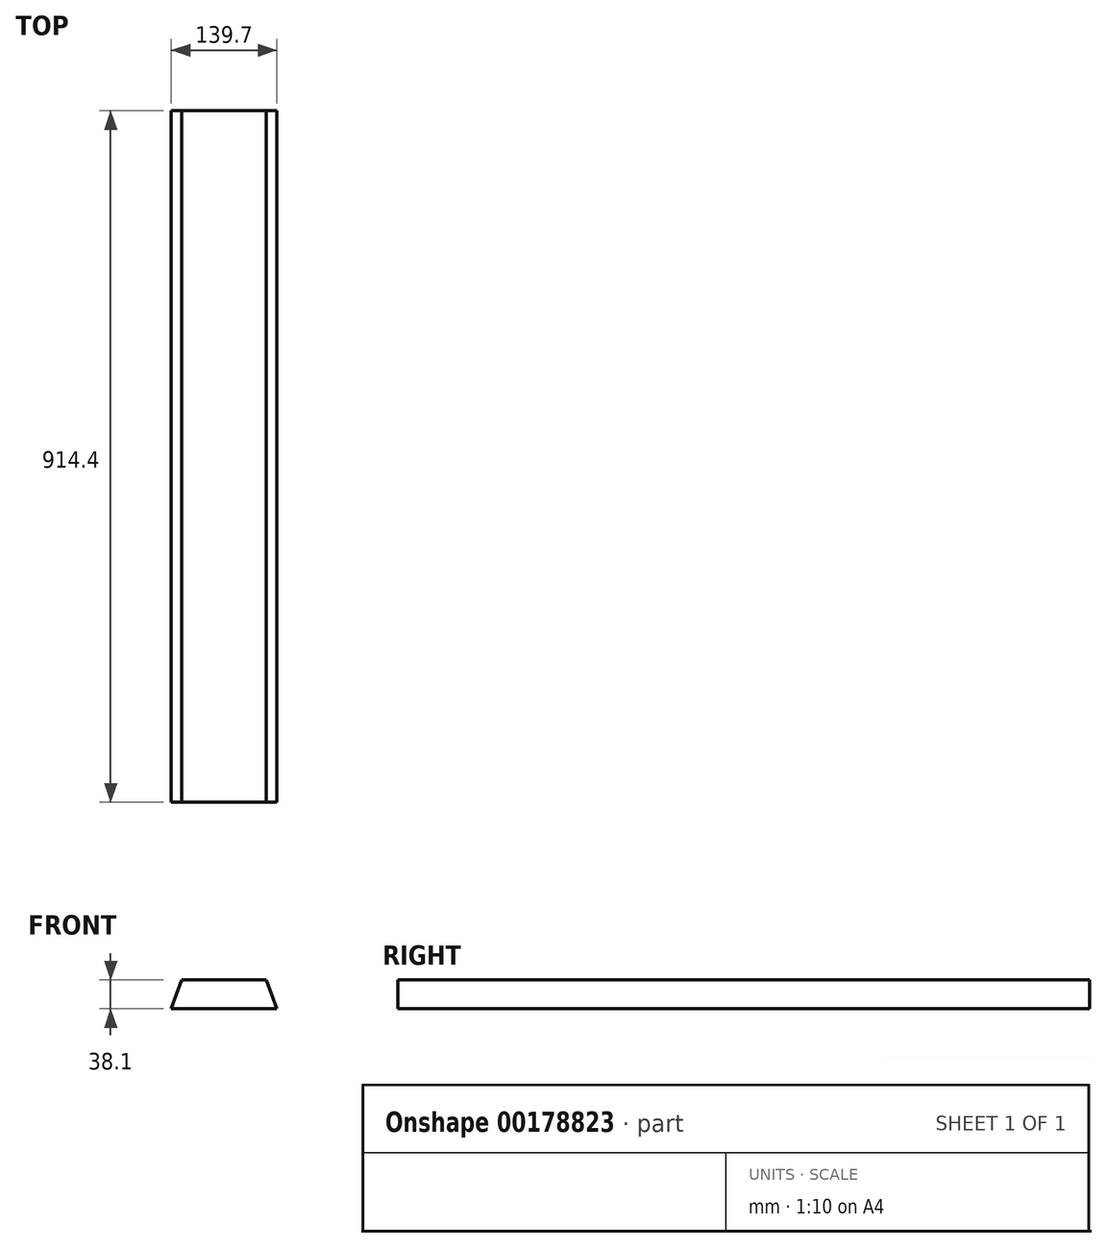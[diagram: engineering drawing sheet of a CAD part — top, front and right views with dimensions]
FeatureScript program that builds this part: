
annotation { "Feature Type Name" : "Feature", "Feature Type Description" : "" }
export const myFeature = defineFeature(function(context is Context, id is Id, definition is map)
    precondition{}
    {
        {
            var Q0;
            Q0=qCreatedBy(makeId("Front.planeOp"),FACE);
            var sketch = newSketch(context, id + "F0", { "sketchPlane" : qUnion([Q0])});
            skLineSegment(sketch, "E0.bottom", {"start": v(0, 0) * mm, "end": v(139.7, 0) * mm});
            skLineSegment(sketch, "E0.top", {"start": v(0, 38.1) * mm, "end": v(139.7, 38.1) * mm});
            skLineSegment(sketch, "E0.left", {"start": v(0, 0) * mm, "end": v(0, 38.1) * mm});
            skLineSegment(sketch, "E0.right", {"start": v(139.7, 0) * mm, "end": v(139.7, 38.1) * mm});
            skSolve(sketch);
        }
        {
            var Q0;
            Q0 = qSketchRegion(id + "F0", true);
            extrude(context, id + "F1", {"entities" : qUnion([Q0]), "depth" : 914.4 * mm});
        }
        {
            var Q0;
            Q0=makeQuery(id+"F1.opExtrude","CAP_FACE",FACE,{"disambiguationData":[OSD([sQuery(id+"F0.wireOp",EDGE,"E0.bottom"),sQuery(id+"F0.wireOp",EDGE,"E0.top"),sQuery(id+"F0.wireOp",EDGE,"E0.left"),sQuery(id+"F0.wireOp",EDGE,"E0.right")])],"isStart":false});
            var sketch = newSketch(context, id + "F2", { "sketchPlane" : qUnion([Q0])});
            skLineSegment(sketch, "E1", {"start": v(0, 0) * mm, "end": v(13.87, 38.1) * mm});
            skLineSegment(sketch, "E2", {"start": v(13.87, 38.1) * mm, "end": v(0, 38.1) * mm});
            skLineSegment(sketch, "E3", {"start": v(0, 38.1) * mm, "end": v(0, 0) * mm});
            skLineSegment(sketch, "E4", {"start": v(139.7, 0) * mm, "end": v(125.83, 38.1) * mm});
            skLineSegment(sketch, "E5", {"start": v(125.83, 38.1) * mm, "end": v(139.7, 38.1) * mm});
            skLineSegment(sketch, "E6", {"start": v(139.7, 38.1) * mm, "end": v(139.7, 0) * mm});
            skSolve(sketch);
        }
        {
            var Q0;
            Q0 = qSketchRegion(id + "F2", true);
            extrude(context, id + "F3", {"entities" : qUnion([Q0]), "operationType" : NewBodyOperationType.REMOVE, "oppositeDirection" : true, "depth" : 914.4 * mm});
        }
    });
